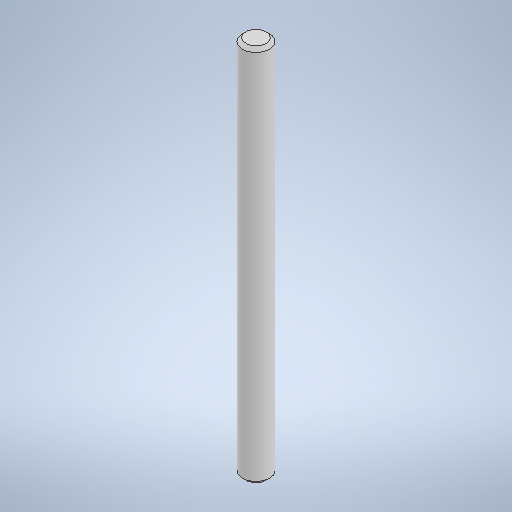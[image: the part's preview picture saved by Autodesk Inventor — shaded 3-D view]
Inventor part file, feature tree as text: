
AUTODESK INVENTOR PART (.ipt)
format: ipt  version: 2025.1 (Build 291241000, 241)  size: 248,320 bytes
history: native  units: mm
features: extrude x1, chamfer x1, sketch x1
ambient origin geometry x8: Origin, YZ Plane, XZ Plane, XY Plane, X Axis, Y Axis, Z Axis, Center Point
bodies: Solid1 (feature_tree)
feature tree (3):
  extrude  "Extrusion1"  Depth=28.0mm TaperAngle=0.0deg
  chamfer  "Chamfer1"  Distance=0.25mm Angle=45.0deg
  sketch  "Sketch1"  dims[d0=2.0mm d1=28.0mm d2=0.0mm d3=0.25mm d4=2.0mm d5=45.0deg]
